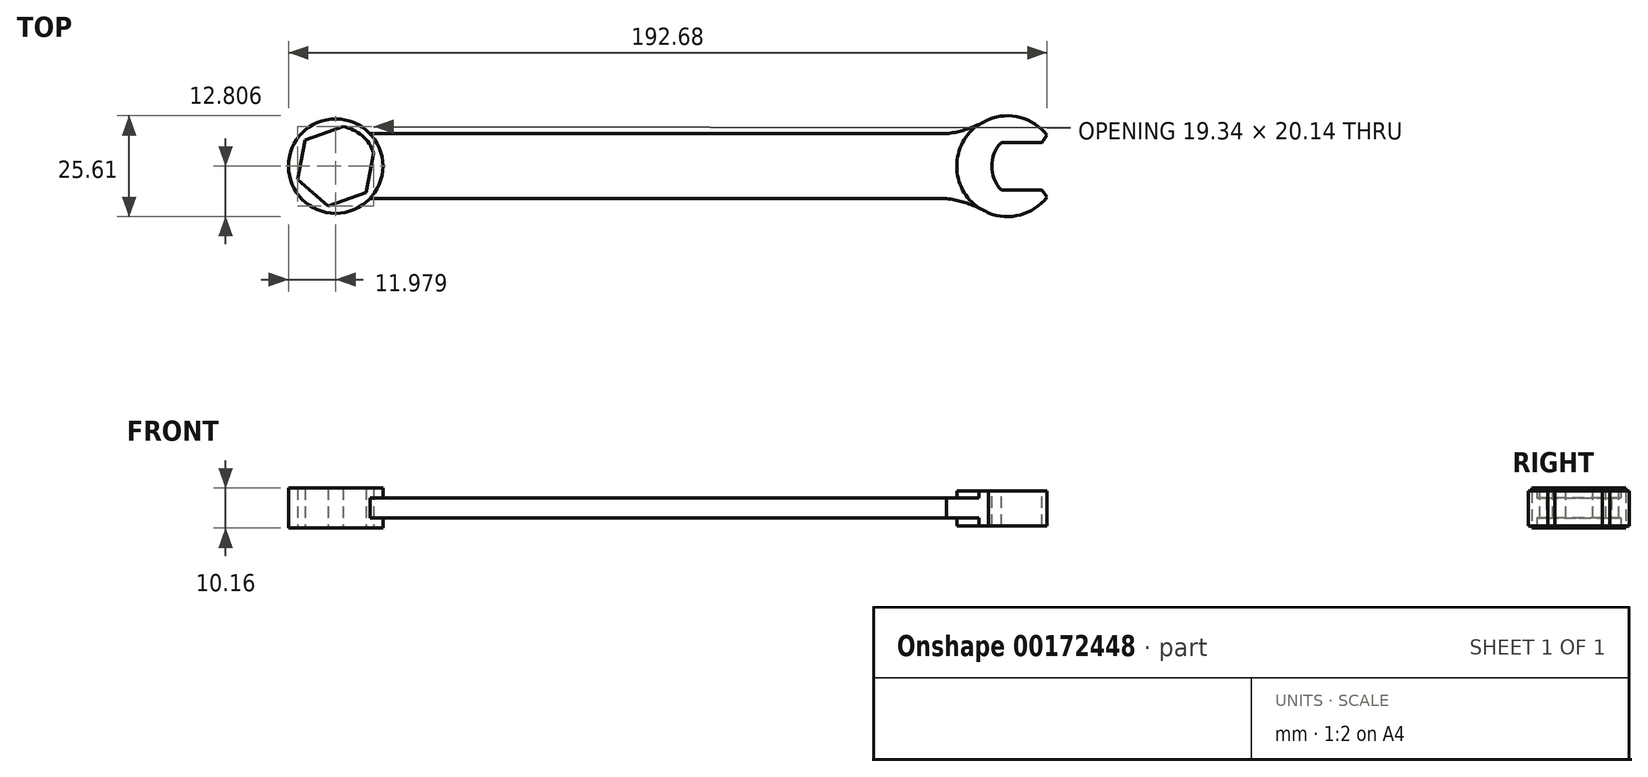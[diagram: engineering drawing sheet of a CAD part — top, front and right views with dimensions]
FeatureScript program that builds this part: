
annotation { "Feature Type Name" : "Feature", "Feature Type Description" : "" }
export const myFeature = defineFeature(function(context is Context, id is Id, definition is map)
    precondition{}
    {
        {
            var Q0;
            Q0=qCreatedBy(makeId("Top.planeOp"),FACE);
            var sketch = newSketch(context, id + "F0", { "sketchPlane" : qUnion([Q0])});
            skLineSegment(sketch, "E0", {"start": v(-73.49, -10.77) * mm, "end": v(78.91, -10.77) * mm});
            skLineSegment(sketch, "E1", {"start": v(-73.49, 5.74) * mm, "end": v(78.91, 5.74) * mm});
            skLineSegment(sketch, "E2", {"start": v(-73.49, 5.74) * mm, "end": v(-73.49, -10.77) * mm});
            skCircle(sketch, "E3", {"center": v(-82.16, -2.51) * mm, "radius": 11.98 * mm});
            skPoint(sketch, "E3.centerSnap0", {"position": v(-73.49, -2.51) * mm});
            skCircle(sketch, "E4", {"center": v(-82.16, -2.51) * mm, "radius": 10.25 * mm});
            skCircle(sketch, "E5.cCircle", {"center": v(-82.16, -2.51) * mm, "radius": 10.25 * mm, "construction": true});
            skLineSegment(sketch, "E5.0", {"start": v(-74.39, -9.2) * mm, "end": v(-84.06, -12.58) * mm});
            skLineSegment(sketch, "E5.1", {"start": v(-84.06, -12.58) * mm, "end": v(-91.83, -5.9) * mm});
            skLineSegment(sketch, "E5.2", {"start": v(-91.83, -5.9) * mm, "end": v(-89.93, 4.17) * mm});
            skLineSegment(sketch, "E5.3", {"start": v(-89.93, 4.17) * mm, "end": v(-80.26, 7.56) * mm});
            skLineSegment(sketch, "E5.4", {"start": v(-80.26, 7.56) * mm, "end": v(-72.5, 0.88) * mm});
            skLineSegment(sketch, "E5.5", {"start": v(-72.5, 0.88) * mm, "end": v(-74.39, -9.2) * mm});
            skLineSegment(sketch, "E6", {"start": v(78.91, 5.74) * mm, "end": v(78.91, -10.77) * mm});
            skCircle(sketch, "E7", {"center": v(88.44, -2.51) * mm, "radius": 12.8 * mm});
            skPoint(sketch, "E7.centerSnap0", {"position": v(78.91, -2.51) * mm});
            skArc(sketch, "E8", {"start": v(73.02, 5.74) * mm, "mid": v(78.54, 7) * mm, "end": v(83.67, 9.37) * mm});
            skArc(sketch, "E9", {"start": v(83.67, -14.4) * mm, "mid": v(78.54, -12.02) * mm, "end": v(73.02, -10.77) * mm});
            skSolve(sketch);
        }
        {
            var Q0;
            {var subQ6=sQuery(id+"F0.wireOp",EDGE,"E0");var subQ7=makeQuery(id+"F0.imprint","INTERSECT",VERTEX,{"derivedFrom":[subQ6,sQuery(id+"F0.wireOp",EDGE,"E9")]});Q0=makeQuery(id+"F0.imprint","IMPRINT",FACE,{"disambiguationData":[TD([[makeQuery(id+"F0.imprint","IMPRINT",EDGE,{"disambiguationData":[TD([[subQ7,1.0]])],"derivedFrom":subQ6}),1.0]])]});}
            var Q1;
            {var subQ0=sQuery(id+"F0.wireOp",EDGE,"E9");var subQ1=sQuery(id+"F0.wireOp",EDGE,"E0");var subQ2=makeQuery(id+"F0.imprint","INTERSECT",VERTEX,{"derivedFrom":[subQ1,subQ0]});Q1=makeQuery(id+"F0.imprint","IMPRINT",FACE,{"disambiguationData":[TD([[makeQuery(id+"F0.imprint","IMPRINT",EDGE,{"disambiguationData":[TD([[subQ2,-1.0]])],"derivedFrom":subQ1}),-1.0]])]});}
            var Q2;
            {var subQ0=sQuery(id+"F0.wireOp",EDGE,"E8");var subQ1=sQuery(id+"F0.wireOp",EDGE,"E1");var subQ2=makeQuery(id+"F0.imprint","INTERSECT",VERTEX,{"derivedFrom":[subQ1,subQ0]});Q2=makeQuery(id+"F0.imprint","IMPRINT",FACE,{"disambiguationData":[TD([[makeQuery(id+"F0.imprint","IMPRINT",EDGE,{"disambiguationData":[TD([[subQ2,-1.0]])],"derivedFrom":subQ1}),1.0]])]});}
            extrude(context, id + "F1", {"entities" : qUnion([Q0, Q1, Q2]), "depth" : 5.08 * mm});
        }
        {
            var Q0;
            {var subQ0=sQuery(id+"F0.wireOp",EDGE,"E2");var subQ1=sQuery(id+"F0.wireOp",EDGE,"E0");var subQ2=makeQuery(id+"F0.imprint","INTERSECT",VERTEX,{"derivedFrom":[subQ1,subQ0]});Q0=makeQuery(id+"F0.imprint","IMPRINT",FACE,{"disambiguationData":[TD([[makeQuery(id+"F0.imprint","IMPRINT",EDGE,{"disambiguationData":[TD([[subQ2,-1.0]])],"derivedFrom":subQ1}),1.0]])]});}
            var Q1;
            {var subQ0=sQuery(id+"F0.wireOp",EDGE,"E5.5");var subQ1=sQuery(id+"F0.wireOp",EDGE,"E2");var subQ2=makeQuery(id+"F0.imprint","INTERSECT",VERTEX,{"derivedFrom":[subQ1,subQ0]});Q1=makeQuery(id+"F0.imprint","IMPRINT",FACE,{"disambiguationData":[TD([[makeQuery(id+"F0.imprint","IMPRINT",EDGE,{"disambiguationData":[TD([[subQ2,-1.0]])],"derivedFrom":subQ1}),1.0]])]});}
            var Q2;
            {var subQ0=sQuery(id+"F0.wireOp",EDGE,"E5.5");var subQ1=sQuery(id+"F0.wireOp",EDGE,"E2");var subQ2=makeQuery(id+"F0.imprint","INTERSECT",VERTEX,{"derivedFrom":[subQ1,subQ0]});Q2=makeQuery(id+"F0.imprint","IMPRINT",FACE,{"disambiguationData":[TD([[makeQuery(id+"F0.imprint","IMPRINT",EDGE,{"disambiguationData":[TD([[subQ2,-1.0]])],"derivedFrom":subQ1}),-1.0]])]});}
            var Q3;
            {var subQ6=sQuery(id+"F0.wireOp",EDGE,"E2");var subQ7=sQuery(id+"F0.wireOp",EDGE,"E0");var subQ8=makeQuery(id+"F0.imprint","INTERSECT",VERTEX,{"derivedFrom":[subQ7,subQ6]});Q3=makeQuery(id+"F0.imprint","IMPRINT",FACE,{"disambiguationData":[TD([[makeQuery(id+"F0.imprint","IMPRINT",EDGE,{"disambiguationData":[TD([[subQ8,-1.0]])],"derivedFrom":subQ7}),-1.0]])]});}
            var Q4;
            {var subQ0=sQuery(id+"F0.wireOp",EDGE,"E5.0");Q4=makeQuery(id+"F0.imprint","IMPRINT",FACE,{"disambiguationData":[TD([[makeQuery(id+"F0.imprint","IMPRINT",EDGE,{"derivedFrom":subQ0}),1.0]])]});}
            var Q5;
            {var subQ0=sQuery(id+"F0.wireOp",EDGE,"E5.1");Q5=makeQuery(id+"F0.imprint","IMPRINT",FACE,{"disambiguationData":[TD([[makeQuery(id+"F0.imprint","IMPRINT",EDGE,{"derivedFrom":subQ0}),1.0]])]});}
            var Q6;
            {var subQ0=sQuery(id+"F0.wireOp",EDGE,"E4");var subQ1=sQuery(id+"F0.wireOp",EDGE,"E2");var subQ2=makeQuery(id+"F0.imprint","INTERSECT",VERTEX,{"disambiguationData":[OD(0.0)],"derivedFrom":[subQ1,subQ0]});Q6=makeQuery(id+"F0.imprint","IMPRINT",FACE,{"disambiguationData":[TD([[makeQuery(id+"F0.imprint","IMPRINT",EDGE,{"disambiguationData":[TD([[subQ2,-1.0]])],"derivedFrom":subQ1}),-1.0]])]});}
            var Q7;
            {var subQ0=sQuery(id+"F0.wireOp",EDGE,"E4");var subQ1=sQuery(id+"F0.wireOp",EDGE,"E2");var subQ2=makeQuery(id+"F0.imprint","INTERSECT",VERTEX,{"disambiguationData":[OD(0.0)],"derivedFrom":[subQ1,subQ0]});Q7=makeQuery(id+"F0.imprint","IMPRINT",FACE,{"disambiguationData":[TD([[makeQuery(id+"F0.imprint","IMPRINT",EDGE,{"disambiguationData":[TD([[subQ2,-1.0]])],"derivedFrom":subQ1}),1.0]])]});}
            var Q8;
            {var subQ0=sQuery(id+"F0.wireOp",EDGE,"E5.2");Q8=makeQuery(id+"F0.imprint","IMPRINT",FACE,{"disambiguationData":[TD([[makeQuery(id+"F0.imprint","IMPRINT",EDGE,{"derivedFrom":subQ0}),1.0]])]});}
            var Q9;
            {var subQ0=sQuery(id+"F0.wireOp",EDGE,"E5.3");Q9=makeQuery(id+"F0.imprint","IMPRINT",FACE,{"disambiguationData":[TD([[makeQuery(id+"F0.imprint","IMPRINT",EDGE,{"derivedFrom":subQ0}),1.0]])]});}
            extrude(context, id + "F2", {"entities" : qUnion([Q0, Q1, Q2, Q3, Q4, Q5, Q6, Q7, Q8, Q9]), "operationType" : NewBodyOperationType.ADD, "depth" : 7.62 * mm, "hasSecondDirection" : true, "secondDirectionOppositeDirection" : true, "secondDirectionDepth" : 2.54 * mm});
        }
        {
            var Q0;
            {var subQ0=sQuery(id+"F0.wireOp",EDGE,"E6");Q0=makeQuery(id+"F0.imprint","IMPRINT",FACE,{"disambiguationData":[TD([[makeQuery(id+"F0.imprint","IMPRINT",EDGE,{"derivedFrom":subQ0}),1.0]])]});}
            var Q1;
            {var subQ0=sQuery(id+"F0.wireOp",EDGE,"E6");Q1=makeQuery(id+"F0.imprint","IMPRINT",FACE,{"disambiguationData":[TD([[makeQuery(id+"F0.imprint","IMPRINT",EDGE,{"derivedFrom":subQ0}),-1.0]])]});}
            extrude(context, id + "F3", {"entities" : qUnion([Q0, Q1]), "operationType" : NewBodyOperationType.ADD, "depth" : 6.86 * mm, "hasSecondDirection" : true, "secondDirectionOppositeDirection" : true, "secondDirectionDepth" : 2.03 * mm});
        }
        {
            var Q0;
            Q0=makeQuery(id+"F3.opExtrude","CAP_FACE",FACE,{"disambiguationData":[OSD([sQuery(id+"F0.wireOp",EDGE,"E7"),sQuery(id+"F0.wireOp",EDGE,"E8"),sQuery(id+"F0.wireOp",EDGE,"E9")])],"isStart":false});
            var sketch = newSketch(context, id + "F4", { "sketchPlane" : qUnion([Q0])});
            skLineSegment(sketch, "E10", {"start": v(98.54, 5.37) * mm, "end": v(97.3, 3.5) * mm});
            skLineSegment(sketch, "E11", {"start": v(98.54, -10.4) * mm, "end": v(97.3, -8.55) * mm});
            skLineSegment(sketch, "E12", {"start": v(97.3, -8.55) * mm, "end": v(86.95, -8.55) * mm});
            skLineSegment(sketch, "E13", {"start": v(97.3, 3.5) * mm, "end": v(86.95, 3.5) * mm});
            skArc(sketch, "E14", {"start": v(86.95, 3.5) * mm, "mid": v(84.5, -2.52) * mm, "end": v(86.95, -8.55) * mm});
            skArc(sketch, "E15", {"start": v(98.54, -10.4) * mm, "mid": v(101.28, -2.51) * mm, "end": v(98.54, 5.37) * mm});
            skSolve(sketch);
        }
        {
            var Q0;
            {var subQ0=sQuery(id+"F4.wireOp",EDGE,"E15");Q0=makeQuery(id+"F4.imprint","IMPRINT",FACE,{"disambiguationData":[TD([[makeQuery(id+"F4.imprint","IMPRINT",EDGE,{"derivedFrom":subQ0}),1.0]])]});}
            var Q1;
            {var subQ1=sQuery(id+"F4.wireOp",EDGE,"E10");Q1=makeQuery(id+"F4.imprint","IMPRINT",FACE,{"disambiguationData":[TD([[makeQuery(id+"F4.imprint","IMPRINT",EDGE,{"derivedFrom":subQ1}),1.0]])]});}
            extrude(context, id + "F5", {"entities" : qUnion([Q0, Q1]), "operationType" : NewBodyOperationType.REMOVE, "oppositeDirection" : true, "depth" : 25.4 * mm});
        }
    });
